# Revit family: CADS_Vent-Axia_Lo-CarbonSentinelHorizontal300ZH
name_source: partatom
category: Mechanical Equipment
revit_build: Autodesk Revit 2015 (Build: 20160512_1515(x64)
units: mm (PartAtom-declared; Revit-internal decimal feet)

## types (1)
- 300ZH
    Apparent Load = 690 VA
    AssetType = Fixed
    C = 301 mm  [stored 0.987533 ft]
    Category = Pr_60_60_36:Heat recovery distribution equipment
    Color = Galvanised steel
    Description = Lo-Carbon Sentinel Kinetic Horizontal
    DurationUnit = year
    E = 184 mm  [stored 0.603675 ft]
    ExpectedLife = 20
    F = 179 mm  [stored 0.58727 ft]
    Features = Summer By-Pass/Humidistat
    G = 187 mm  [stored 0.613517 ft]
    H = 102 mm
    I = 279 mm
    IfcExportAs = IfcAirToAirHeatRecoveryType
    IfcExportType = USERDEFINED
    J = 174 mm  [stored 0.570866 ft]
    K = 187 mm  [stored 0.613517 ft]
    Manufacturer = Vent-Axia Limited
    Material = Galvanised steel
    Model = Kinetic Horizontal 300ZH
    ModelNumber = 449536
    ModelReference = Kinetic Horizontal 300ZH
    Name = MVHR Unit
    NominalHeight = 301 mm  [stored 0.987533 ft]
    NominalLength = 940 mm  [stored 3.08399 ft]
    NominalWidth = 720 mm  [stored 2.3622 ft]
    NumberOfPoles = 1
    RatedCurrent = 3 A
    RatedVoltage = 230 V
    Shape = Rectangular
    Size = 720mm x 940mm x 301mm 
570mm x 849mm x 200mm
    SpigotDiameter = 150 mm
    SpigotLength = 204 mm  [stored 0.669291 ft]
    SpigotWidth = 60 mm  [stored 0.19685 ft]
    Version = 1.0
    WarrantyDurationLabor = 2
    WarrantyDurationMotors = 5
    WarrantyDurationParts = 2
    WarrantyDurationUnit = year

note: [stored X ft] marks values corroborated as IEEE doubles in the binary element streams (Revit-internal decimal feet)

## geometry (parser evidence)
native form markers: Sweep x15
no freeform markers — native parametric forms only
